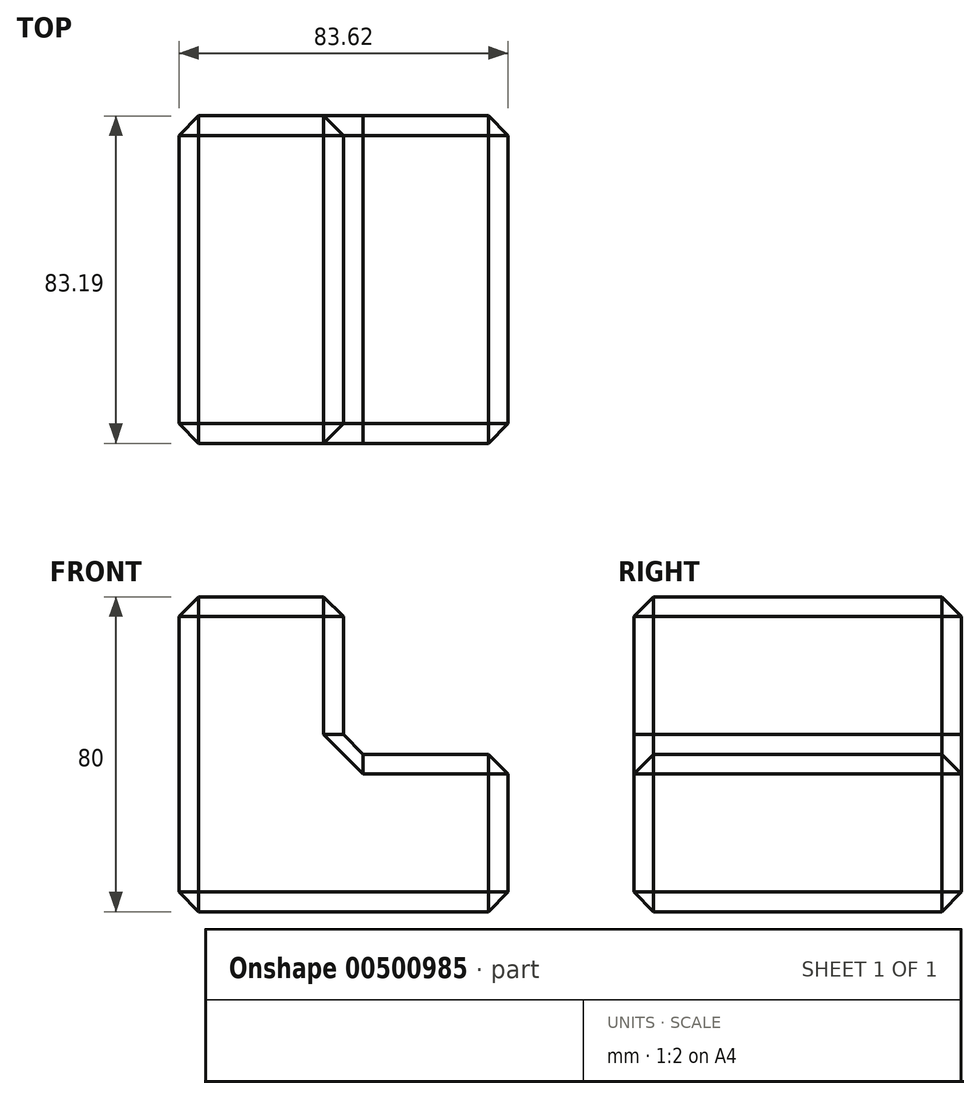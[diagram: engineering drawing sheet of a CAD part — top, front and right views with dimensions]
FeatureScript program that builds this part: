
annotation { "Feature Type Name" : "Feature", "Feature Type Description" : "" }
export const myFeature = defineFeature(function(context is Context, id is Id, definition is map)
    precondition{}
    {
        {
            var Q0;
            Q0=qCreatedBy(makeId("Top.planeOp"),FACE);
            var sketch = newSketch(context, id + "F0", { "sketchPlane" : qUnion([Q0])});
            skLineSegment(sketch, "E0.bottom", {"start": v(-59.13, -45.93) * mm, "end": v(24.5, -45.93) * mm});
            skLineSegment(sketch, "E0.top", {"start": v(-59.13, 37.26) * mm, "end": v(24.5, 37.26) * mm});
            skLineSegment(sketch, "E0.left", {"start": v(-59.13, -45.93) * mm, "end": v(-59.13, 37.26) * mm});
            skLineSegment(sketch, "E0.right", {"start": v(24.5, -45.93) * mm, "end": v(24.5, 37.26) * mm});
            skSolve(sketch);
        }
        {
            var Q0;
            Q0=makeQuery(id+"F0.imprint","IMPRINT",FACE,{"disambiguationData":[TD([[makeQuery(id+"F0.imprint","IMPRINT",EDGE,{"derivedFrom":sQuery(id+"F0.wireOp",EDGE,"E0.bottom")}),1.0]])]});
            extrude(context, id + "F1", {"entities" : qUnion([Q0]), "depth" : 40 * mm});
        }
        {
            var Q0;
            Q0=makeQuery(id+"F1.opExtrude","CAP_FACE",FACE,{"disambiguationData":[OSD([sQuery(id+"F0.wireOp",EDGE,"E0.bottom"),sQuery(id+"F0.wireOp",EDGE,"E0.top"),sQuery(id+"F0.wireOp",EDGE,"E0.left"),sQuery(id+"F0.wireOp",EDGE,"E0.right")])],"isStart":false});
            var sketch = newSketch(context, id + "F2", { "sketchPlane" : qUnion([Q0])});
            skLineSegment(sketch, "E1", {"start": v(-17.32, 37.26) * mm, "end": v(-17.32, -45.93) * mm});
            skSolve(sketch);
        }
        {
            var Q0;
            {var subQ1=sQuery(id+"F2.wireOp",EDGE,"E1");Q0=makeQuery(id+"F2.imprint","IMPRINT",FACE,{"disambiguationData":[TD([[makeQuery(id+"F2.imprint","IMPRINT",EDGE,{"derivedFrom":subQ1}),-1.0]])]});}
            extrude(context, id + "F3", {"entities" : qUnion([Q0]), "operationType" : NewBodyOperationType.ADD, "depth" : 40 * mm});
        }
        {
            var Q0;
            Q0=makeQuery(id+"F3.opExtrude","CAP_FACE",FACE,{"disambiguationData":[OSD([sQuery(id+"F0.wireOp",EDGE,"E0.bottom"),sQuery(id+"F0.wireOp",EDGE,"E0.top"),sQuery(id+"F0.wireOp",EDGE,"E0.left"),sQuery(id+"F2.wireOp",EDGE,"E1")])],"isStart":false});
            var Q1;
            Q1=makeQuery(id+"F3.opExtrude","SWEPT_FACE",FACE,{"disambiguationData":[OSD([sQuery(id+"F2.wireOp",EDGE,"E1")])]});
            var Q2;
            Q2=makeQuery(id+"F1.opExtrude","CAP_FACE",FACE,{"disambiguationData":[OSD([sQuery(id+"F0.wireOp",EDGE,"E0.bottom"),sQuery(id+"F0.wireOp",EDGE,"E0.top"),sQuery(id+"F0.wireOp",EDGE,"E0.left"),sQuery(id+"F0.wireOp",EDGE,"E0.right")])],"isStart":false});
            var Q3;
            {var subQ0=sQuery(id+"F0.wireOp",EDGE,"E0.bottom");Q3=makeQuery(id+"F3.boolean.opBoolean","MERGE",FACE,{"derivedFrom":[makeQuery(id+"F1.opExtrude","SWEPT_FACE",FACE,{"disambiguationData":[OSD([subQ0])]}),makeQuery(id+"F3.opExtrude","SWEPT_FACE",FACE,{"disambiguationData":[OSD([subQ0])]})]});}
            var Q4;
            Q4=makeQuery(id+"F1.opExtrude","SWEPT_FACE",FACE,{"disambiguationData":[OSD([sQuery(id+"F0.wireOp",EDGE,"E0.right")])]});
            var Q5;
            {var subQ0=sQuery(id+"F0.wireOp",EDGE,"E0.top");Q5=makeQuery(id+"F3.boolean.opBoolean","MERGE",FACE,{"derivedFrom":[makeQuery(id+"F1.opExtrude","SWEPT_FACE",FACE,{"disambiguationData":[OSD([subQ0])]}),makeQuery(id+"F3.opExtrude","SWEPT_FACE",FACE,{"disambiguationData":[OSD([subQ0])]})]});}
            var Q6;
            {var subQ0=sQuery(id+"F0.wireOp",EDGE,"E0.left");Q6=makeQuery(id+"F3.boolean.opBoolean","MERGE",FACE,{"derivedFrom":[makeQuery(id+"F1.opExtrude","SWEPT_FACE",FACE,{"disambiguationData":[OSD([subQ0])]}),makeQuery(id+"F3.opExtrude","SWEPT_FACE",FACE,{"disambiguationData":[OSD([subQ0])]})]});}
            var Q7;
            Q7=makeQuery(id+"F1.opExtrude","CAP_FACE",FACE,{"disambiguationData":[OSD([sQuery(id+"F0.wireOp",EDGE,"E0.bottom"),sQuery(id+"F0.wireOp",EDGE,"E0.top"),sQuery(id+"F0.wireOp",EDGE,"E0.left"),sQuery(id+"F0.wireOp",EDGE,"E0.right")])],"isStart":true});
            chamfer(context, id + "F4", {"entities" : qUnion([Q0, Q1, Q2, Q3, Q4, Q5, Q6, Q7]), "width" : 5 * mm, "tangentPropagation" : true});
        }
    });
